# Revit family: Steni - Panel - Colour
name_source: partatom
category: Generic Models
revit_build: Autodesk Revit Architecture 2014 (Build: 20131024_2115(x64)
units: mm (PartAtom-declared; Revit-internal decimal feet)

## types (60) — shared parameters
Allowable Variation = ± 2 mm
BIMobject Category = Cladding
BIMobject QR code url = http://steni.bimobject.com
Density = Apprx. 1880 Kg/m³
Design country = Norway
Diagonal Deviation = 3 mm
Drilling Distance Tolerance = ± 5 mm
Edge Straightness Full Size = 1 mm
Edition number = 1
Elasticity Module = 5000 MPa
Flexural Strength = 40 MPa
Front Side Of Panel = ELECTRON CURED ACRYL
Heat Conductivity = 0.55 W/m°C
Heat Resistance = 0.0074 m²°C/W
Humidity Altered Dimension = 5.2 X 106 m/m x%RF
IFC Classification = Covering
Impact Strength = 20 KJ / m 2
Impermeability = 100%
Manufacturer = Steni
Manufacturer URL = www.steni.com
Manufacturer country = Norway
Name of the object = Steni - Panel - Colour
No Damage = 300 CYCLE
NominalHeight = 1195
NominalWidth = 3500
Penetration Of Water Vapour = 3,3 X 10-12 Kg/m²sPa
Product family = Steni Colour
Reverse Side Of Panel = GLASS FIBER SURFACING VEIL
Standard Length = 3500 mm  [stored 11.4829 ft]
Standard Width = 1195 mm  [stored 3.9206 ft]
Temperature Expansion (-20° +65°) = 0.026 mm/m°C
Tensile Strength = 15 N/mm²
UNSPC Category = Siding and exterior wall materials
UNSPC code = 301518
URL = http://steni.bimobject.com
Visual Assessment = 3 M / 90°
Water Absorbtion After 28 days = <1.5 %
Weight Net (kg) = 11 Kg/m²

## per-type parameters (varying)
| type | Gloss Count On Surface | Installation instructions | Model | Product SKU | Product certification | Product data url | Product group | Steni Material | Technical description |
| Steni - Panel - DUO | HG, HM, or M | http://steni.bimobject.com | Steni - Panel - Coulour Type 6 | sc123 |  | http://www.steni.co.uk | FS 100 | Steni_Aluminum | http://steni.bimobject.com |
| SN 9402 | HG, HM or M | http://steni.com | Steni - Panel - Colour | SN9402 | http://steni.co.uk | http://steni.co.uk | Colour | Steni - SN 9402• S 2010-R90B | http://steni.co.uk |
| SN 9401 | HG, HM or M | http://steni.com | Steni - Panel - Colour | SN9401 | http://steni.co.uk | http://steni.co.uk | Colour | Steni - SN 9401• S 8010-R90B | http://steni.co.uk |
| SN 9400 | HG, HM or M | http://steni.com | Steni - Panel - Colour | SN9400 | http://steni.co.uk | http://steni.co.uk | Colour | Steni - SN 9400• S 4050-R90B | http://steni.co.uk |
| SN 9310 | HG, HM or M | http://steni.com | Steni - Panel - Colour | SN9310 | http://steni.co.uk | http://steni.co.uk | Colour | Steni - SN 9310• S 2010-B30G | http://steni.co.uk |
| SN 9309 | HG, HM or M | http://steni.com | Steni - Panel - Colour | SN9309 | http://steni.co.uk | http://steni.co.uk | Colour | Steni - SN 9309• S 5010-B30G | http://steni.co.uk |
| SN 9308 | HG, HM or M | http://steni.com | Steni - Panel - Colour | SN9308 | http://steni.co.uk | http://steni.co.uk | Colour | Steni - SN 9308• S 2010-G30Y | http://steni.co.uk |
| SN 9307 | HG, HM or M | http://steni.com | Steni - Panel - Colour | SN9307 | http://steni.co.uk | http://steni.co.uk | Colour | Steni - SN 9307• S 5010-G30Y | http://steni.co.uk |
| SN 9306 | HG, HM | http://steni.com | Steni - Panel - Colour | SN9306 | http://steni.co.uk | http://steni.co.uk | Colour | Steni - SN 9306• S 8505-G20Y | http://steni.co.uk |
| SN 9305 | HG, HM or M | http://steni.com | Steni - Panel - Colour | SN9305 | http://steni.co.uk | http://steni.co.uk | Colour | Steni - SN 9305• S 0540-B30G | http://steni.co.uk |
| SN 9304 | HG, HM or M | http://steni.com | Steni - Panel - Colour | SN9304 | http://steni.co.uk | http://steni.co.uk | Colour | Steni - SN 9304• S 5040-B30G | http://steni.co.uk |
| SN 9303 | HG, HM or M | http://steni.com | Steni - Panel - Colour | SN9303 | http://steni.co.uk | http://steni.co.uk | Colour | Steni - SN 9303• S 6530-B30G | http://steni.co.uk |
| SN 9302 | HG, HM or M | http://steni.com | Steni - Panel - Colour | SN9302 | http://steni.co.uk | http://steni.co.uk | Colour | Steni - SN 9302• S 0565-G50Y | http://steni.co.uk |
| SN 9301 | HG, HM or M | http://steni.com | Steni - Panel - Colour | SN9301 | http://steni.co.uk | http://steni.co.uk | Colour | Steni - SN 9301• S 4550-G30Y | http://steni.co.uk |
| SN 9300 | HG, HM or M | http://steni.com | Steni - Panel - Colour | SN9300 | http://steni.co.uk | http://steni.co.uk | Colour | Steni - SN 9300• S 1070-G30Y | http://steni.co.uk |
| SN 9207 | HG, HM or M | http://steni.com | Steni - Panel - Colour | SN9207 | http://steni.co.uk | http://steni.co.uk | Colour | Steni - SN 9207• S 5010-Y30R | http://steni.co.uk |
| SN 9206 | HG, HM or M | http://steni.com | Steni - Panel - Colour | SN9206 | http://steni.co.uk | http://steni.co.uk | Colour | Steni - SN 9206• S 5010-Y10R | http://steni.co.uk |
| SN 9205 | HG, HM or M | http://steni.com | Steni - Panel - Colour | SN9205 | http://steni.co.uk | http://steni.co.uk | Colour | Steni - SN 9205• S 1502-Y | http://steni.co.uk |
| SN 9204 | HG, HM or M | http://steni.com | Steni - Panel - Colour | SN9204 | http://steni.co.uk | http://steni.co.uk | Colour | Steni - SN 9204 • S 8505-G80Y | http://steni.co.uk |
| SN 9203 | HG, HM | http://steni.com | Steni - Panel - Colour | SN9203 | http://steni.co.uk | http://steni.co.uk | Colour | Steni - SN 9203 • S 7020-Y50R | http://steni.co.uk |
| SN 9202 | HG, HM | http://steni.com | Steni - Panel - Colour | SN9202 | http://steni.co.uk | http://steni.co.uk | Colour | Steni - SN 9202 • S 4550-Y30R | http://steni.co.uk |
| SN 9201 | HG, HM | http://steni.com | Steni - Panel - Colour | SN9201 | http://steni.co.uk | http://steni.co.uk | Colour | Steni - SN 9201 • S 0560-G80Y | http://steni.co.uk |
| SN 9200 | HG, HM | http://steni.com | Steni - Panel - Colour | SN9200 | http://steni.co.uk | http://steni.co.uk | Colour | Steni - SN 9200 • S 1070-Y10R | http://steni.co.uk |
| SN 9109 | HG, HM | http://steni.com | Steni - Panel - Colour | SN9109 | http://steni.co.uk | http://steni.co.uk | Colour | Steni - SN 9109 • S 1050-R | http://steni.co.uk |
| SN 9108 | HG, HM or M | http://steni.com | Steni - Panel - Colour | SN9108 | http://steni.co.uk | http://steni.co.uk | Colour | Steni - SN 9108 • S 5010-R70B | http://steni.co.uk |
| SN 9107 | HG, HM or M | http://steni.com | Steni - Panel - Colour | SN9107 | http://steni.co.uk | http://steni.co.uk | Colour | Steni - SN 9107 • S 5030-R60B | http://steni.co.uk |
| SN 9106 | HG, HM or M | http://steni.com | Steni - Panel - Colour | SN9106 | http://steni.co.uk | http://steni.co.uk | Colour | Steni - SN 9106 • S 3010-R50B | http://steni.co.uk |
| SN 9105 | HG, HM or M | http://steni.com | Steni - Panel - Colour | SN9105 | http://steni.co.uk | http://steni.co.uk | Colour | Steni - SN 9105 • S 1020-R30B | http://steni.co.uk |
| SN 9104 | HG, HM | http://steni.com | Steni - Panel - Colour | SN9104 | http://steni.co.uk | http://steni.co.uk | Colour | Steni - SN 9104 • S 4030-R20B | http://steni.co.uk |
| SN 9103 | HG, HM or M | http://steni.com | Steni - Panel - Colour | SN9103 | http://steni.co.uk | http://steni.co.uk | Colour | Steni - SN 9103 • S 7020-R | http://steni.co.uk |
| SN 9102 | HG, HM | http://steni.com | Steni - Panel - Colour | SN9102 | http://steni.co.uk | http://steni.co.uk | Colour | Steni - SN 9102 • S 0580-Y40R | http://steni.co.uk |
| SN 9101 | HG, HM | http://steni.com | Steni - Panel - Colour | SN9101 | http://steni.co.uk | http://steni.co.uk | Colour | Steni - SN 9101• S 2070-Y60R | http://steni.co.uk |
| SN 9100 | HG, HM | http://steni.com | Steni - Panel - Colour | SN9100 | http://steni.co.uk | http://steni.co.uk | Colour | Steni - SN 9100• S 1580-Y90R | http://steni.co.uk |
| SN 7534 | HG, HM, or M | http://steni.com | Steni - Panel - Colour | SN7534 | http://steni.co.uk | http://steni.co.uk | Colour | Steni - SN 7534• S 5040-R80B | http://steni.co.uk |
| SN 7020 | HG, HM, or M | http://steni.com | Steni - Panel - Colour | SN7020 | http://steni.co.uk | http://steni.co.uk | Colour | Steni - SN 7020• S 5010-R90B | http://steni.co.uk |
| SN 7013 | HG, HM, or M | http://steni.com | Steni - Panel - Colour | SN7013 | http://steni.co.uk | http://steni.co.uk | Colour | Steni - SN 7013• S 2010-R70B | http://steni.co.uk |
| SN 6520 | HG, HM, or M | http://steni.com | Steni - Panel - Colour | SN6520 | http://steni.co.uk | http://steni.co.uk | Colour | Steni - SN 6520• S 3020-B10G | http://steni.co.uk |
| SN 6510 | HG, HM, or M | http://steni.com | Steni - Panel - Colour | SN6510 | http://steni.co.uk | http://steni.co.uk | Colour | Steni - SN 6510• S 2005-B20G | http://steni.co.uk |
| SN 5550 | HG, HM, or M | http://steni.com | Steni - Panel - Colour | SN5550 | http://steni.co.uk | http://steni.co.uk | Colour | Steni - SN 5550• S 2040-B10G | http://steni.co.uk |
| SN 5010 | HG, HM, or M | http://steni.com | Steni - Panel - Colour | SN5010 | http://steni.co.uk | http://steni.co.uk | Colour | Steni - SN 5010• S 4010-G10Y | http://steni.co.uk |
| SN 4500 | HG, HM, or M | http://steni.com | Steni - Panel - Colour | SN4500 | http://steni.co.uk | http://steni.co.uk | Colour | Steni - SN 4500• S 2020-Y40R | http://steni.co.uk |
| SN 4357 | HG, HM, or M | http://steni.com | Steni - Panel - Colour | SN4357 | http://steni.co.uk | http://steni.co.uk | Colour | Steni - SN 4357• S 3030-Y50R | http://steni.co.uk |
| SN 4353 | HG, HM, or M | http://steni.com | Steni - Panel - Colour | SN4353 | http://steni.co.uk | http://steni.co.uk | Colour | Steni - SN 4353• S 3010-Y50R | http://steni.co.uk |
| SN 4350 | HG, HM, or M | http://steni.com | Steni - Panel - Colour | SN4350 | http://steni.co.uk | http://steni.co.uk | Colour | Steni - SN 4350• S 3010-Y30R | http://steni.co.uk |
| SN 4072 | HG, HM, or M | http://steni.com | Steni - Panel - Colour | SN4072 | http://steni.co.uk | http://steni.co.uk | Colour | Steni - SN 4072• S 2010-Y10R | http://steni.co.uk |
| SN 4012 | HG, HM, or M | http://steni.com | Steni - Panel - Colour | SN4012 | http://steni.co.uk | http://steni.co.uk | Colour | Steni - SN 4012• S 2010-Y30R | http://steni.co.uk |
| SN 3413 | HG, HM, or M | http://steni.com | Steni - Panel - Colour | SN3413 | http://steni.co.uk | http://steni.co.uk | Colour | Steni - SN 3413• S 1020-Y10R | http://steni.co.uk |
| SN 2008 | HG, HM, or M | http://steni.com | Steni - Panel - Colour | SN2008 | http://steni.co.uk | http://steni.co.uk | Colour | Steni - SN 2008• S 4550-Y80R | http://steni.co.uk |
| SN 8013 | HG, HM, or M | http://steni.com | Steni - Panel - Colour | SN8013 | http://steni.co.uk | http://steni.co.uk | Colour | Steni - SN 8013• S 1002-G50Y | http://steni.co.uk |
| SN 8011 | HG, HM, or M | http://steni.com | Steni - Panel - Colour | SN8011 | http://steni.co.uk | http://steni.co.uk | Colour | Steni - SN 8011• S 1005-Y20R | http://steni.co.uk |
| SN 8010 | HG, HM, or M | http://steni.com | Steni - Panel - Colour | SN8010 | http://steni.co.uk | http://steni.co.uk | Colour | Steni - SN 8010• S 0502-Y | http://steni.co.uk |
| SN 8020 | HG, HM, or M | http://steni.com | Steni - Panel - Colour | SN8020 | http://steni.co.uk | http://steni.co.uk | Colour | Steni - SN 8020• S 3000-N | http://steni.co.uk |
| SN 8008 | HG, HM, or M | http://steni.com | Steni - Panel - Colour | SN8008 | http://steni.co.uk | http://steni.co.uk | Colour | Steni - SN 8008• S 8000-N | http://steni.co.uk |
| SN 8007 | HG, HM, or M | http://steni.com | Steni - Panel - Colour | SN8007 | http://steni.co.uk | http://steni.co.uk | Colour | Steni - SN 8007• S 7000-N | http://steni.co.uk |
| SN 8006 | HG, HM, or M | http://steni.com | Steni - Panel - Colour | SN8006 | http://steni.co.uk | http://steni.co.uk | Colour | Steni - SN 8006• S 6000-N | http://steni.co.uk |
| SN 8005 | HG, HM, or M | http://steni.com | Steni - Panel - Colour | SN8005 | http://steni.co.uk | http://steni.co.uk | Colour | Steni - SN 8005• S 5000-N | http://steni.co.uk |
| SN 8004 | HG, HM, or M | http://steni.com | Steni - Panel - Colour | SN8004 | http://steni.co.uk | http://steni.co.uk | Colour | Steni - SN 8004• S 4000-N | http://steni.co.uk |
| SN 8003 | HG, HM, or M | http://steni.com | Steni - Panel - Colour | SN8003 | http://steni.co.uk | http://steni.co.uk | Colour | Steni - SN 8003• S 2000-N | http://steni.co.uk |
| SN 8002 | HG, HM, or M | http://steni.com | Steni - Panel - Colour | SN8002 | http://steni.co.uk | http://steni.co.uk | Colour | Steni - SN 8002• S 1000-N | http://steni.co.uk |
| SN 8001 | HG, HM, or M | http://steni.com | Steni - Panel - Colour | SN8001 | http://steni.co.uk | http://steni.co.uk | Colour | Steni - SN 8001• S 0500-N | http://steni.co.uk |

note: [stored X ft] marks values corroborated as IEEE doubles in the binary element streams (Revit-internal decimal feet)

## geometry (parser evidence)
native form markers: Sweep x2
no freeform markers — native parametric forms only
